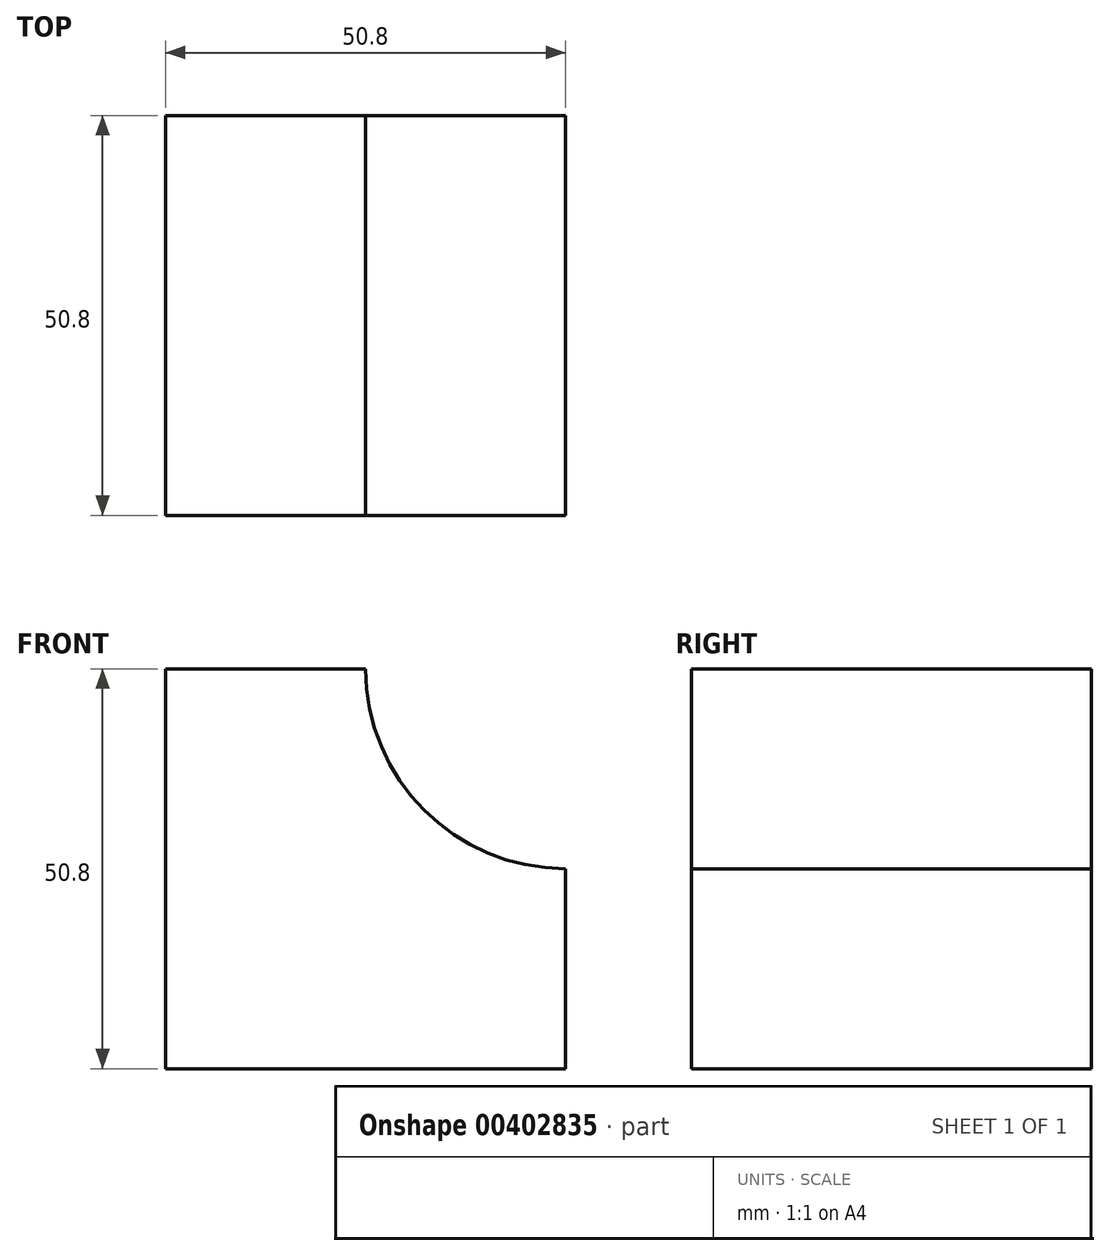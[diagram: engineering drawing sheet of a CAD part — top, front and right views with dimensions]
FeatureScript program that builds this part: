
annotation { "Feature Type Name" : "Feature", "Feature Type Description" : "" }
export const myFeature = defineFeature(function(context is Context, id is Id, definition is map)
    precondition{}
    {
        {
            var Q0;
            Q0=qCreatedBy(makeId("Front.planeOp"),FACE);
            var sketch = newSketch(context, id + "F0", { "sketchPlane" : qUnion([Q0])});
            skLineSegment(sketch, "E0", {"start": v(-57.79, 28.87) * mm, "end": v(-57.79, -21.93) * mm});
            skLineSegment(sketch, "E1", {"start": v(-57.79, -21.93) * mm, "end": v(-6.99, -21.93) * mm});
            skLineSegment(sketch, "E2", {"start": v(-57.79, 28.87) * mm, "end": v(-32.39, 28.87) * mm});
            skLineSegment(sketch, "E3", {"start": v(-32.39, 28.87) * mm, "end": v(-32.39, 3.47) * mm});
            skLineSegment(sketch, "E4", {"start": v(-32.39, 3.47) * mm, "end": v(-6.99, 3.47) * mm});
            skLineSegment(sketch, "E5", {"start": v(-6.99, 3.47) * mm, "end": v(-6.99, -21.93) * mm});
            skArc(sketch, "E6", {"start": v(-32.39, 28.87) * mm, "mid": v(-24.95, 10.91) * mm, "end": v(-6.99, 3.47) * mm});
            skSolve(sketch);
        }
        {
            var Q0;
            Q0 = qSketchRegion(id + "F0", true);
            extrude(context, id + "F1", {"entities" : qUnion([Q0]), "depth" : 50.8 * mm});
        }
    });
